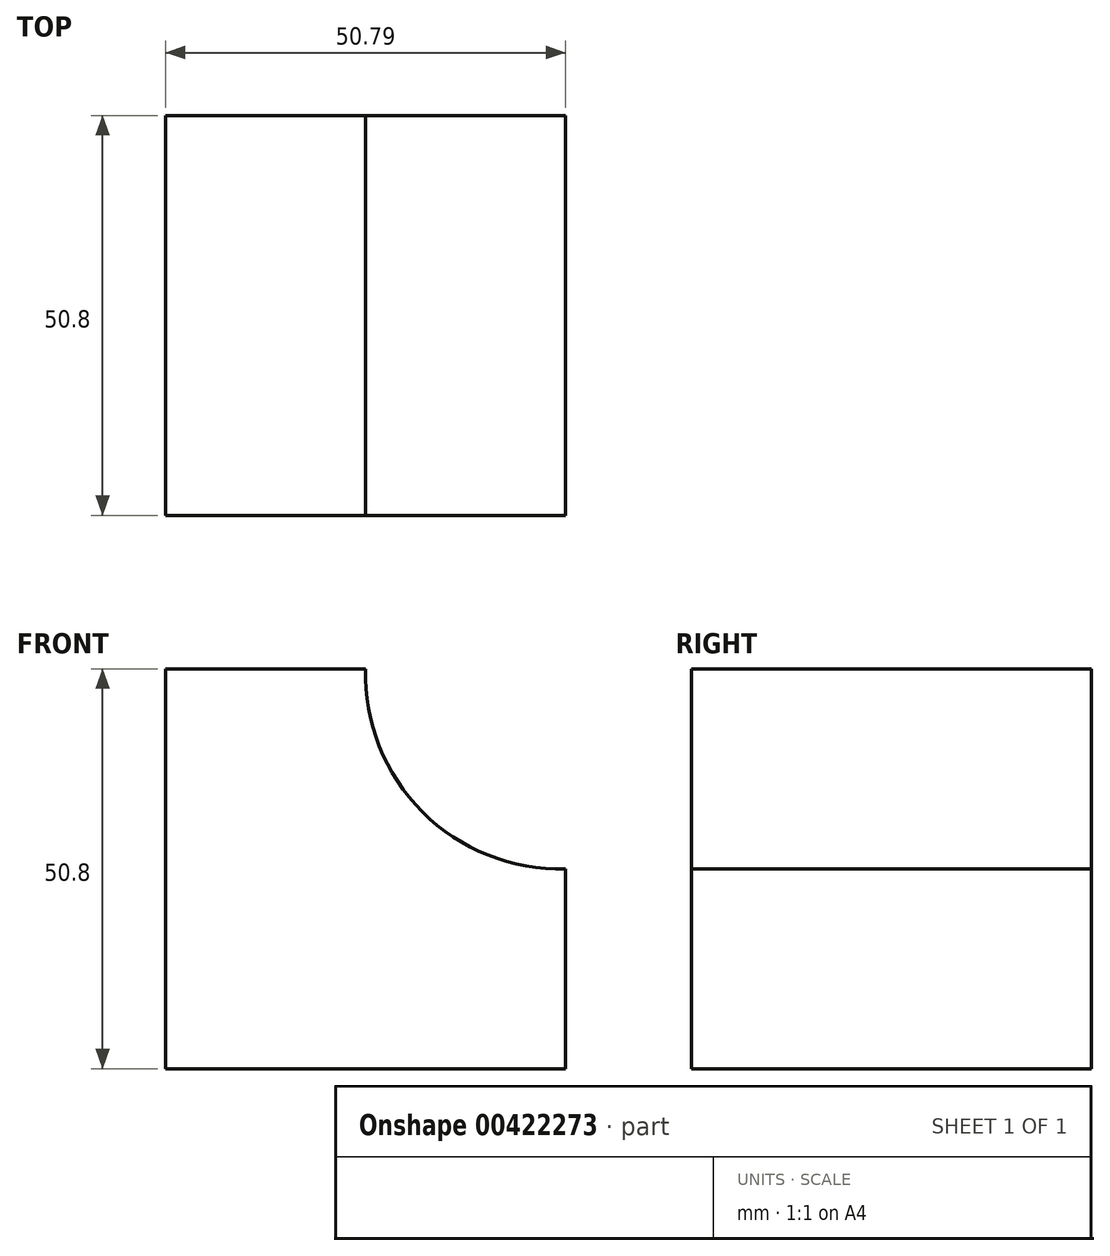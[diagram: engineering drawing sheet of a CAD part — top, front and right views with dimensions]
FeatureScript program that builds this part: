
annotation { "Feature Type Name" : "Feature", "Feature Type Description" : "" }
export const myFeature = defineFeature(function(context is Context, id is Id, definition is map)
    precondition{}
    {
        {
            var Q0;
            Q0=qCreatedBy(makeId("Front.planeOp"),FACE);
            var sketch = newSketch(context, id + "F0", { "sketchPlane" : qUnion([Q0])});
            skLineSegment(sketch, "E0", {"start": v(38.95, -11.84) * mm, "end": v(38.95, -37.24) * mm});
            skLineSegment(sketch, "E1", {"start": v(38.95, -37.24) * mm, "end": v(-11.84, -37.24) * mm});
            skLineSegment(sketch, "E2", {"start": v(-11.84, -37.24) * mm, "end": v(-11.84, 13.56) * mm});
            skLineSegment(sketch, "E3", {"start": v(-11.84, 13.56) * mm, "end": v(13.56, 13.56) * mm});
            skArc(sketch, "E4", {"start": v(13.56, 13.56) * mm, "mid": v(20.78, -4.62) * mm, "end": v(38.95, -11.84) * mm});
            skSolve(sketch);
        }
        {
            var Q0;
            Q0=makeQuery(id+"F0.imprint","IMPRINT",FACE,{"disambiguationData":[TD([[makeQuery(id+"F0.imprint","IMPRINT",EDGE,{"derivedFrom":sQuery(id+"F0.wireOp",EDGE,"E0")}),-1.0]])]});
            extrude(context, id + "F1", {"entities" : qUnion([Q0]), "depth" : 50.8 * mm});
        }
    });
